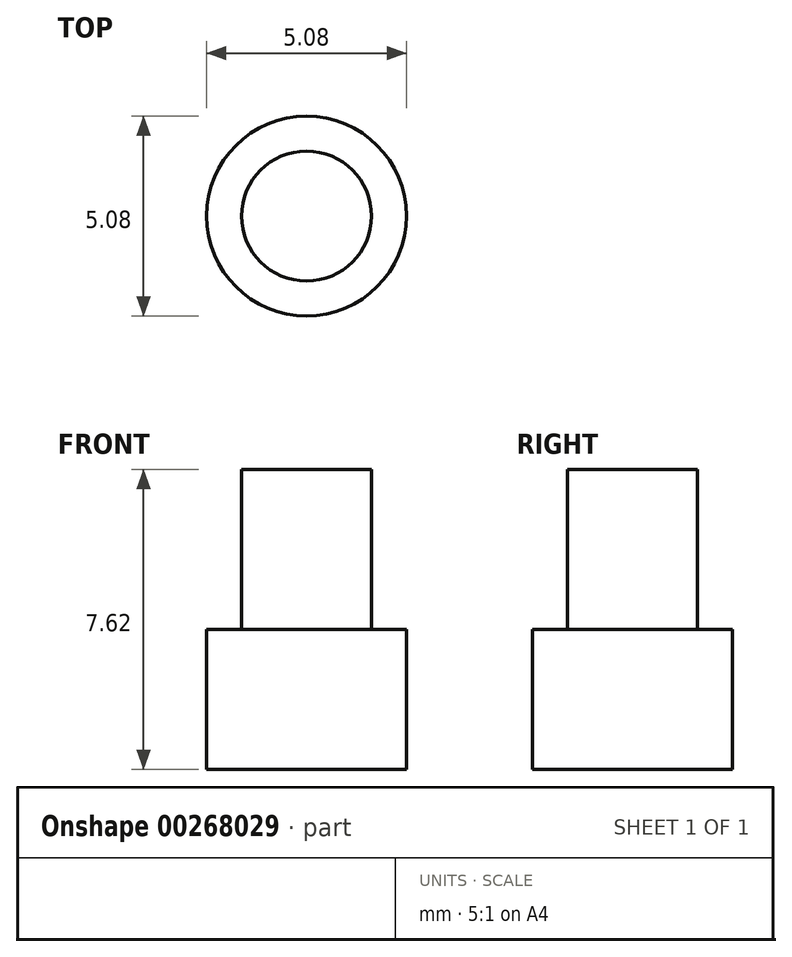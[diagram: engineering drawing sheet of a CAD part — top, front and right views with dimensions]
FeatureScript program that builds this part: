
annotation { "Feature Type Name" : "Feature", "Feature Type Description" : "" }
export const myFeature = defineFeature(function(context is Context, id is Id, definition is map)
    precondition{}
    {
        {
            var Q0;
            Q0=qCreatedBy(makeId("Top.planeOp"),FACE);
            var sketch = newSketch(context, id + "F0", { "sketchPlane" : qUnion([Q0])});
            skCircle(sketch, "E0", {"center": v(0, 0) * mm, "radius": 2.54 * mm});
            skSolve(sketch);
        }
        {
            var Q0;
            Q0 = qSketchRegion(id + "F0", true);
            var Q1;
            Q1=makeQuery(id+"F0.imprint","IMPRINT",FACE,{"disambiguationData":[TD([[makeQuery(id+"F0.imprint","IMPRINT",EDGE,{"derivedFrom":sQuery(id+"F0.wireOp",EDGE,"E0")}),1.0]])]});
            extrude(context, id + "F1", {"entities" : qUnion([Q0, Q1]), "depth" : 3.56 * mm, "offsetDistance" : 25.4 * mm});
        }
        {
            var Q0;
            Q0=makeQuery(id+"F1.opExtrude","CAP_FACE",FACE,{"disambiguationData":[OSD([sQuery(id+"F0.wireOp",EDGE,"E0")])],"isStart":false});
            var sketch = newSketch(context, id + "F2", { "sketchPlane" : qUnion([Q0])});
            skCircle(sketch, "E1", {"center": v(0, 0) * mm, "radius": 1.65 * mm});
            skSolve(sketch);
        }
        {
            var Q0;
            Q0=makeQuery(id+"F2.imprint","IMPRINT",FACE,{"disambiguationData":[TD([[makeQuery(id+"F2.imprint","IMPRINT",EDGE,{"derivedFrom":sQuery(id+"F2.wireOp",EDGE,"E1")}),1.0]])]});
            extrude(context, id + "F3", {"entities" : qUnion([Q0]), "operationType" : NewBodyOperationType.ADD, "depth" : 4.06 * mm, "offsetDistance" : 25.4 * mm});
        }
    });
